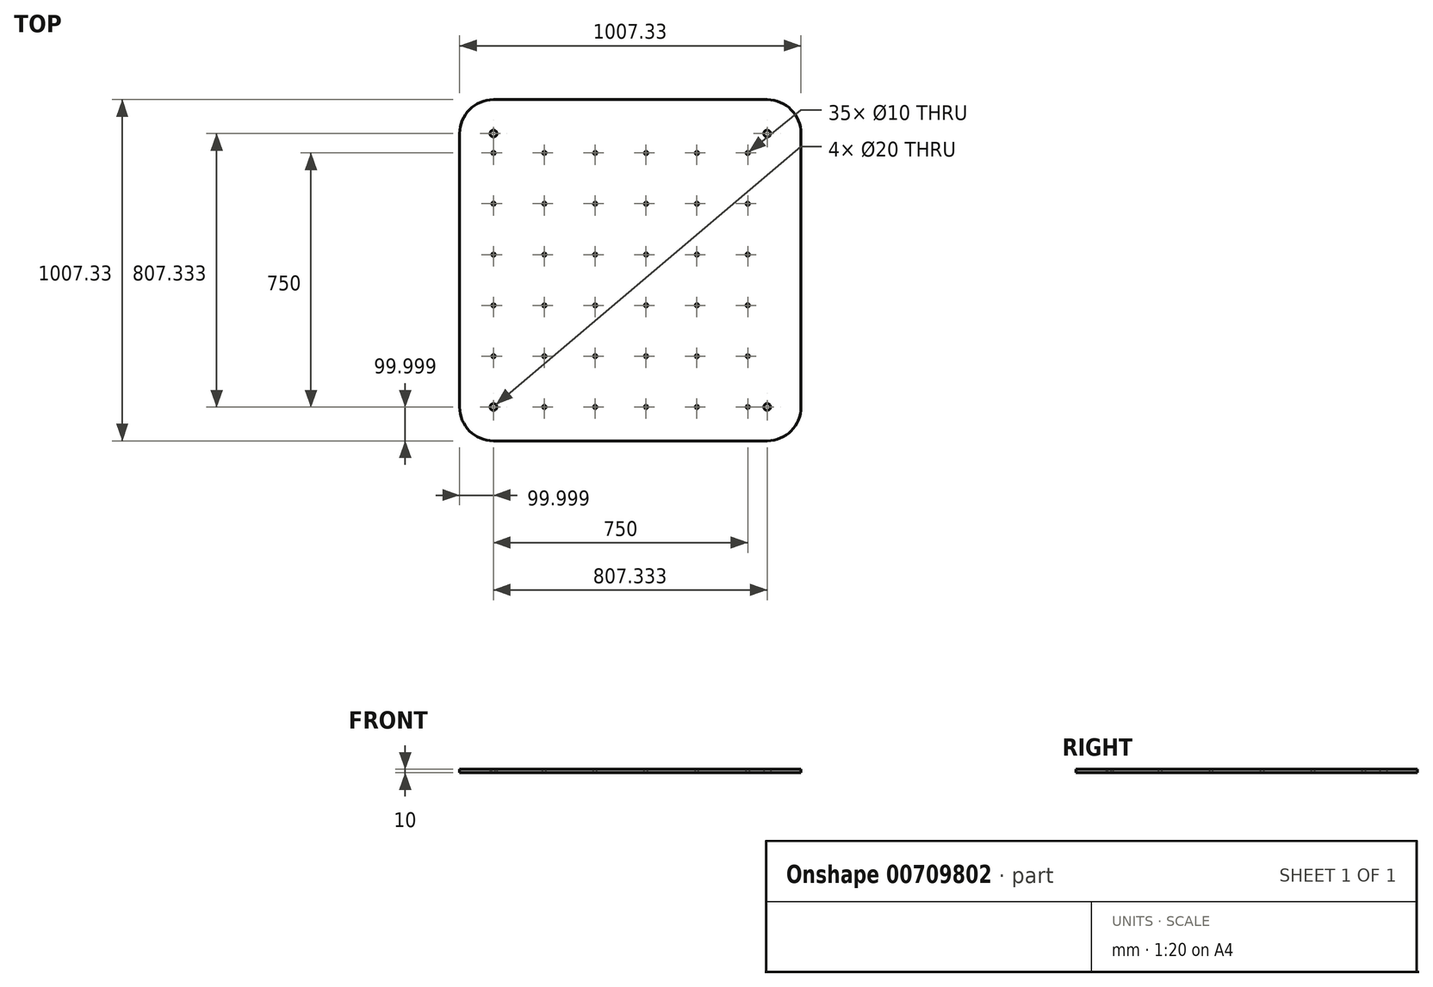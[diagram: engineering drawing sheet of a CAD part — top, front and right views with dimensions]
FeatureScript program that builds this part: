
annotation { "Feature Type Name" : "Feature", "Feature Type Description" : "" }
export const myFeature = defineFeature(function(context is Context, id is Id, definition is map)
    precondition{}
    {
        {
            var Q0;
            Q0=qCreatedBy(makeId("Top.planeOp"),FACE);
            var sketch = newSketch(context, id + "F0", { "sketchPlane" : qUnion([Q0])});
            skLineSegment(sketch, "E0.bottom", {"start": v(-368.41, -251.86) * mm, "end": v(438.92, -251.86) * mm});
            skLineSegment(sketch, "E0.top", {"start": v(-368.41, 555.47) * mm, "end": v(438.92, 555.47) * mm});
            skLineSegment(sketch, "E0.left", {"start": v(-368.41, -251.86) * mm, "end": v(-368.41, 555.47) * mm});
            skLineSegment(sketch, "E0.right", {"start": v(438.92, -251.86) * mm, "end": v(438.92, 555.47) * mm});
            skCircle(sketch, "E1", {"center": v(-368.41, 555.47) * mm, "radius": 10 * mm});
            skCircle(sketch, "E2", {"center": v(-368.41, -251.86) * mm, "radius": 10 * mm});
            skCircle(sketch, "E3", {"center": v(438.92, -251.86) * mm, "radius": 10 * mm});
            skCircle(sketch, "E4", {"center": v(438.92, 555.47) * mm, "radius": 10 * mm});
            skLineSegment(sketch, "E5.0", {"start": v(-468.41, -251.86) * mm, "end": v(-468.41, 555.47) * mm});
            skLineSegment(sketch, "E5.1", {"start": v(-368.41, -351.86) * mm, "end": v(438.92, -351.86) * mm});
            skLineSegment(sketch, "E5.2", {"start": v(538.92, -251.86) * mm, "end": v(538.92, 555.47) * mm});
            skLineSegment(sketch, "E5.3", {"start": v(-368.41, 655.47) * mm, "end": v(438.92, 655.47) * mm});
            skPoint(sketch, "E6.visualSharp", {"position": v(-468.41, 655.47) * mm});
            skArc(sketch, "E6.filletArc", {"start": v(-368.41, 655.47) * mm, "mid": v(-439.12, 626.18) * mm, "end": v(-468.41, 555.47) * mm});
            skPoint(sketch, "E7.visualSharp", {"position": v(538.92, 655.47) * mm});
            skArc(sketch, "E7.filletArc", {"start": v(538.92, 555.47) * mm, "mid": v(509.63, 626.18) * mm, "end": v(438.92, 655.47) * mm});
            skPoint(sketch, "E8.visualSharp", {"position": v(538.92, -351.86) * mm});
            skArc(sketch, "E8.filletArc", {"start": v(438.92, -351.86) * mm, "mid": v(509.63, -322.57) * mm, "end": v(538.92, -251.86) * mm});
            skPoint(sketch, "E9.visualSharp", {"position": v(-468.41, -351.86) * mm});
            skArc(sketch, "E9.filletArc", {"start": v(-468.41, -251.86) * mm, "mid": v(-439.12, -322.57) * mm, "end": v(-368.41, -351.86) * mm});
            skSolve(sketch);
        }
        {
            var Q0;
            Q0=makeQuery(id+"F0.imprint","IMPRINT",FACE,{"disambiguationData":[TD([[makeQuery(id+"F0.imprint","IMPRINT",EDGE,{"derivedFrom":sQuery(id+"F0.wireOp",EDGE,"E5.0")}),-1.0]])]});
            var Q1;
            {var subQ5=sQuery(id+"F0.wireOp",EDGE,"E2");var subQ13=sQuery(id+"F0.wireOp",EDGE,"E0.bottom");var subQ14=makeQuery(id+"F0.imprint","INTERSECT",VERTEX,{"derivedFrom":[subQ13,subQ5]});Q1=makeQuery(id+"F0.imprint","IMPRINT",FACE,{"disambiguationData":[TD([[makeQuery(id+"F0.imprint","IMPRINT",EDGE,{"disambiguationData":[TD([[subQ14,-1.0]])],"derivedFrom":subQ13}),1.0]])]});}
            extrude(context, id + "F1", {"entities" : qUnion([Q0, Q1]), "depth" : 10 * mm, "offsetDistance" : 25 * mm});
        }
        {
            var Q0;
            Q0=makeQuery(id+"F1.opExtrude","CAP_FACE",FACE,{"disambiguationData":[OSD([sQuery(id+"F0.wireOp",EDGE,"E1"),sQuery(id+"F0.wireOp",EDGE,"E2"),sQuery(id+"F0.wireOp",EDGE,"E3"),sQuery(id+"F0.wireOp",EDGE,"E4"),sQuery(id+"F0.wireOp",EDGE,"E5.0"),sQuery(id+"F0.wireOp",EDGE,"E5.1"),sQuery(id+"F0.wireOp",EDGE,"E5.2"),sQuery(id+"F0.wireOp",EDGE,"E5.3"),sQuery(id+"F0.wireOp",EDGE,"E6.filletArc"),sQuery(id+"F0.wireOp",EDGE,"E7.filletArc"),sQuery(id+"F0.wireOp",EDGE,"E8.filletArc"),sQuery(id+"F0.wireOp",EDGE,"E9.filletArc")])],"isStart":false});
            var sketch = newSketch(context, id + "F2", { "sketchPlane" : qUnion([Q0])});
            skLineSegment(sketch, "E10", {"start": v(-368.41, -251.86) * mm, "end": v(-218.41, -251.86) * mm});
            skCircle(sketch, "E11", {"center": v(-218.41, -251.86) * mm, "radius": 5 * mm});
            skCircle(sketch, "E12.0.1.0", {"center": v(-218.41, -101.86) * mm, "radius": 5 * mm});
            skCircle(sketch, "E12.0.2.0", {"center": v(-218.41, 48.14) * mm, "radius": 5 * mm});
            skCircle(sketch, "E12.0.3.0", {"center": v(-218.41, 198.14) * mm, "radius": 5 * mm});
            skCircle(sketch, "E12.0.4.0", {"center": v(-218.41, 348.14) * mm, "radius": 5 * mm});
            skCircle(sketch, "E12.0.5.0", {"center": v(-218.41, 498.14) * mm, "radius": 5 * mm});
            skCircle(sketch, "E12.1.0.0", {"center": v(-68.41, -251.86) * mm, "radius": 5 * mm});
            skCircle(sketch, "E12.1.1.0", {"center": v(-68.41, -101.86) * mm, "radius": 5 * mm});
            skCircle(sketch, "E12.1.2.0", {"center": v(-68.41, 48.14) * mm, "radius": 5 * mm});
            skCircle(sketch, "E12.1.3.0", {"center": v(-68.41, 198.14) * mm, "radius": 5 * mm});
            skCircle(sketch, "E12.1.4.0", {"center": v(-68.41, 348.14) * mm, "radius": 5 * mm});
            skCircle(sketch, "E12.1.5.0", {"center": v(-68.41, 498.14) * mm, "radius": 5 * mm});
            skCircle(sketch, "E12.2.0.0", {"center": v(81.59, -251.86) * mm, "radius": 5 * mm});
            skCircle(sketch, "E12.2.1.0", {"center": v(81.59, -101.86) * mm, "radius": 5 * mm});
            skCircle(sketch, "E12.2.2.0", {"center": v(81.59, 48.14) * mm, "radius": 5 * mm});
            skCircle(sketch, "E12.2.3.0", {"center": v(81.59, 198.14) * mm, "radius": 5 * mm});
            skCircle(sketch, "E12.2.4.0", {"center": v(81.59, 348.14) * mm, "radius": 5 * mm});
            skCircle(sketch, "E12.2.5.0", {"center": v(81.59, 498.14) * mm, "radius": 5 * mm});
            skCircle(sketch, "E12.3.0.0", {"center": v(231.59, -251.86) * mm, "radius": 5 * mm});
            skCircle(sketch, "E12.3.1.0", {"center": v(231.59, -101.86) * mm, "radius": 5 * mm});
            skCircle(sketch, "E12.3.2.0", {"center": v(231.59, 48.14) * mm, "radius": 5 * mm});
            skCircle(sketch, "E12.3.3.0", {"center": v(231.59, 198.14) * mm, "radius": 5 * mm});
            skCircle(sketch, "E12.3.4.0", {"center": v(231.59, 348.14) * mm, "radius": 5 * mm});
            skCircle(sketch, "E12.3.5.0", {"center": v(231.59, 498.14) * mm, "radius": 5 * mm});
            skCircle(sketch, "E12.4.0.0", {"center": v(381.59, -251.86) * mm, "radius": 5 * mm});
            skCircle(sketch, "E12.4.1.0", {"center": v(381.59, -101.86) * mm, "radius": 5 * mm});
            skCircle(sketch, "E12.4.2.0", {"center": v(381.59, 48.14) * mm, "radius": 5 * mm});
            skCircle(sketch, "E12.4.3.0", {"center": v(381.59, 198.14) * mm, "radius": 5 * mm});
            skCircle(sketch, "E12.4.4.0", {"center": v(381.59, 348.14) * mm, "radius": 5 * mm});
            skCircle(sketch, "E12.4.5.0", {"center": v(381.59, 498.14) * mm, "radius": 5 * mm});
            skLineSegment(sketch, "E12.direction1", {"start": v(-218.41, -251.86) * mm, "end": v(-68.41, -251.86) * mm, "construction": true});
            skLineSegment(sketch, "E12.direction2", {"start": v(-218.41, -251.86) * mm, "end": v(-218.41, -101.86) * mm, "construction": true});
            skCircle(sketch, "E13.1.0.0", {"center": v(-368.41, 498.14) * mm, "radius": 5 * mm});
            skCircle(sketch, "E13.1.0.1", {"center": v(-368.41, 348.14) * mm, "radius": 5 * mm});
            skCircle(sketch, "E13.1.0.2", {"center": v(-368.41, 198.14) * mm, "radius": 5 * mm});
            skCircle(sketch, "E13.1.0.3", {"center": v(-368.41, 48.14) * mm, "radius": 5 * mm});
            skCircle(sketch, "E13.1.0.4", {"center": v(-368.41, -101.86) * mm, "radius": 5 * mm});
            skLineSegment(sketch, "E13.direction1", {"start": v(-218.41, 498.14) * mm, "end": v(-368.41, 498.14) * mm, "construction": true});
            skSolve(sketch);
        }
        {
            var Q0;
            Q0=makeQuery(id+"F2.imprint","IMPRINT",FACE,{"disambiguationData":[TD([[makeQuery(id+"F2.imprint","IMPRINT",EDGE,{"derivedFrom":sQuery(id+"F2.wireOp",EDGE,"E13.1.0.4")}),1.0]])]});
            var Q1;
            Q1=makeQuery(id+"F2.imprint","IMPRINT",FACE,{"disambiguationData":[TD([[makeQuery(id+"F2.imprint","IMPRINT",EDGE,{"derivedFrom":sQuery(id+"F2.wireOp",EDGE,"E13.1.0.3")}),1.0]])]});
            var Q2;
            Q2=makeQuery(id+"F2.imprint","IMPRINT",FACE,{"disambiguationData":[TD([[makeQuery(id+"F2.imprint","IMPRINT",EDGE,{"derivedFrom":sQuery(id+"F2.wireOp",EDGE,"E12.0.2.0")}),1.0]])]});
            var Q3;
            Q3=makeQuery(id+"F2.imprint","IMPRINT",FACE,{"disambiguationData":[TD([[makeQuery(id+"F2.imprint","IMPRINT",EDGE,{"derivedFrom":sQuery(id+"F2.wireOp",EDGE,"E12.0.1.0")}),1.0]])]});
            var Q4;
            Q4=makeQuery(id+"F2.imprint","IMPRINT",FACE,{"disambiguationData":[TD([[makeQuery(id+"F2.imprint","IMPRINT",EDGE,{"derivedFrom":sQuery(id+"F2.wireOp",EDGE,"E11")}),1.0]])]});
            var Q5;
            Q5=makeQuery(id+"F2.imprint","IMPRINT",FACE,{"disambiguationData":[TD([[makeQuery(id+"F2.imprint","IMPRINT",EDGE,{"derivedFrom":sQuery(id+"F2.wireOp",EDGE,"E12.1.0.0")}),1.0]])]});
            var Q6;
            Q6=makeQuery(id+"F2.imprint","IMPRINT",FACE,{"disambiguationData":[TD([[makeQuery(id+"F2.imprint","IMPRINT",EDGE,{"derivedFrom":sQuery(id+"F2.wireOp",EDGE,"E12.2.0.0")}),1.0]])]});
            var Q7;
            Q7=makeQuery(id+"F2.imprint","IMPRINT",FACE,{"disambiguationData":[TD([[makeQuery(id+"F2.imprint","IMPRINT",EDGE,{"derivedFrom":sQuery(id+"F2.wireOp",EDGE,"E12.1.1.0")}),1.0]])]});
            var Q8;
            Q8=makeQuery(id+"F2.imprint","IMPRINT",FACE,{"disambiguationData":[TD([[makeQuery(id+"F2.imprint","IMPRINT",EDGE,{"derivedFrom":sQuery(id+"F2.wireOp",EDGE,"E12.1.2.0")}),1.0]])]});
            var Q9;
            Q9=makeQuery(id+"F2.imprint","IMPRINT",FACE,{"disambiguationData":[TD([[makeQuery(id+"F2.imprint","IMPRINT",EDGE,{"derivedFrom":sQuery(id+"F2.wireOp",EDGE,"E12.2.1.0")}),1.0]])]});
            var Q10;
            Q10=makeQuery(id+"F2.imprint","IMPRINT",FACE,{"disambiguationData":[TD([[makeQuery(id+"F2.imprint","IMPRINT",EDGE,{"derivedFrom":sQuery(id+"F2.wireOp",EDGE,"E13.1.0.2")}),1.0]])]});
            var Q11;
            Q11=makeQuery(id+"F2.imprint","IMPRINT",FACE,{"disambiguationData":[TD([[makeQuery(id+"F2.imprint","IMPRINT",EDGE,{"derivedFrom":sQuery(id+"F2.wireOp",EDGE,"E12.0.3.0")}),1.0]])]});
            var Q12;
            Q12=makeQuery(id+"F2.imprint","IMPRINT",FACE,{"disambiguationData":[TD([[makeQuery(id+"F2.imprint","IMPRINT",EDGE,{"derivedFrom":sQuery(id+"F2.wireOp",EDGE,"E12.1.3.0")}),1.0]])]});
            var Q13;
            Q13=makeQuery(id+"F2.imprint","IMPRINT",FACE,{"disambiguationData":[TD([[makeQuery(id+"F2.imprint","IMPRINT",EDGE,{"derivedFrom":sQuery(id+"F2.wireOp",EDGE,"E12.2.3.0")}),1.0]])]});
            var Q14;
            Q14=makeQuery(id+"F2.imprint","IMPRINT",FACE,{"disambiguationData":[TD([[makeQuery(id+"F2.imprint","IMPRINT",EDGE,{"derivedFrom":sQuery(id+"F2.wireOp",EDGE,"E12.2.2.0")}),1.0]])]});
            var Q15;
            Q15=makeQuery(id+"F2.imprint","IMPRINT",FACE,{"disambiguationData":[TD([[makeQuery(id+"F2.imprint","IMPRINT",EDGE,{"derivedFrom":sQuery(id+"F2.wireOp",EDGE,"E12.0.4.0")}),1.0]])]});
            var Q16;
            Q16=makeQuery(id+"F2.imprint","IMPRINT",FACE,{"disambiguationData":[TD([[makeQuery(id+"F2.imprint","IMPRINT",EDGE,{"derivedFrom":sQuery(id+"F2.wireOp",EDGE,"E13.1.0.1")}),1.0]])]});
            var Q17;
            Q17=makeQuery(id+"F2.imprint","IMPRINT",FACE,{"disambiguationData":[TD([[makeQuery(id+"F2.imprint","IMPRINT",EDGE,{"derivedFrom":sQuery(id+"F2.wireOp",EDGE,"E13.1.0.0")}),1.0]])]});
            var Q18;
            Q18=makeQuery(id+"F2.imprint","IMPRINT",FACE,{"disambiguationData":[TD([[makeQuery(id+"F2.imprint","IMPRINT",EDGE,{"derivedFrom":sQuery(id+"F2.wireOp",EDGE,"E12.0.5.0")}),1.0]])]});
            var Q19;
            Q19=makeQuery(id+"F2.imprint","IMPRINT",FACE,{"disambiguationData":[TD([[makeQuery(id+"F2.imprint","IMPRINT",EDGE,{"derivedFrom":sQuery(id+"F2.wireOp",EDGE,"E12.1.4.0")}),1.0]])]});
            var Q20;
            Q20=makeQuery(id+"F2.imprint","IMPRINT",FACE,{"disambiguationData":[TD([[makeQuery(id+"F2.imprint","IMPRINT",EDGE,{"derivedFrom":sQuery(id+"F2.wireOp",EDGE,"E12.1.5.0")}),1.0]])]});
            var Q21;
            Q21=makeQuery(id+"F2.imprint","IMPRINT",FACE,{"disambiguationData":[TD([[makeQuery(id+"F2.imprint","IMPRINT",EDGE,{"derivedFrom":sQuery(id+"F2.wireOp",EDGE,"E12.2.4.0")}),1.0]])]});
            var Q22;
            Q22=makeQuery(id+"F2.imprint","IMPRINT",FACE,{"disambiguationData":[TD([[makeQuery(id+"F2.imprint","IMPRINT",EDGE,{"derivedFrom":sQuery(id+"F2.wireOp",EDGE,"E12.2.5.0")}),1.0]])]});
            var Q23;
            Q23=makeQuery(id+"F2.imprint","IMPRINT",FACE,{"disambiguationData":[TD([[makeQuery(id+"F2.imprint","IMPRINT",EDGE,{"derivedFrom":sQuery(id+"F2.wireOp",EDGE,"E12.3.4.0")}),1.0]])]});
            var Q24;
            Q24=makeQuery(id+"F2.imprint","IMPRINT",FACE,{"disambiguationData":[TD([[makeQuery(id+"F2.imprint","IMPRINT",EDGE,{"derivedFrom":sQuery(id+"F2.wireOp",EDGE,"E12.3.5.0")}),1.0]])]});
            var Q25;
            Q25=makeQuery(id+"F2.imprint","IMPRINT",FACE,{"disambiguationData":[TD([[makeQuery(id+"F2.imprint","IMPRINT",EDGE,{"derivedFrom":sQuery(id+"F2.wireOp",EDGE,"E12.4.5.0")}),1.0]])]});
            var Q26;
            Q26=makeQuery(id+"F2.imprint","IMPRINT",FACE,{"disambiguationData":[TD([[makeQuery(id+"F2.imprint","IMPRINT",EDGE,{"derivedFrom":sQuery(id+"F2.wireOp",EDGE,"E12.4.4.0")}),1.0]])]});
            var Q27;
            Q27=makeQuery(id+"F2.imprint","IMPRINT",FACE,{"disambiguationData":[TD([[makeQuery(id+"F2.imprint","IMPRINT",EDGE,{"derivedFrom":sQuery(id+"F2.wireOp",EDGE,"E12.3.3.0")}),1.0]])]});
            var Q28;
            Q28=makeQuery(id+"F2.imprint","IMPRINT",FACE,{"disambiguationData":[TD([[makeQuery(id+"F2.imprint","IMPRINT",EDGE,{"derivedFrom":sQuery(id+"F2.wireOp",EDGE,"E12.4.3.0")}),1.0]])]});
            var Q29;
            Q29=makeQuery(id+"F2.imprint","IMPRINT",FACE,{"disambiguationData":[TD([[makeQuery(id+"F2.imprint","IMPRINT",EDGE,{"derivedFrom":sQuery(id+"F2.wireOp",EDGE,"E12.4.2.0")}),1.0]])]});
            var Q30;
            Q30=makeQuery(id+"F2.imprint","IMPRINT",FACE,{"disambiguationData":[TD([[makeQuery(id+"F2.imprint","IMPRINT",EDGE,{"derivedFrom":sQuery(id+"F2.wireOp",EDGE,"E12.3.2.0")}),1.0]])]});
            var Q31;
            Q31=makeQuery(id+"F2.imprint","IMPRINT",FACE,{"disambiguationData":[TD([[makeQuery(id+"F2.imprint","IMPRINT",EDGE,{"derivedFrom":sQuery(id+"F2.wireOp",EDGE,"E12.3.1.0")}),1.0]])]});
            var Q32;
            Q32=makeQuery(id+"F2.imprint","IMPRINT",FACE,{"disambiguationData":[TD([[makeQuery(id+"F2.imprint","IMPRINT",EDGE,{"derivedFrom":sQuery(id+"F2.wireOp",EDGE,"E12.4.1.0")}),1.0]])]});
            var Q33;
            Q33=makeQuery(id+"F2.imprint","IMPRINT",FACE,{"disambiguationData":[TD([[makeQuery(id+"F2.imprint","IMPRINT",EDGE,{"derivedFrom":sQuery(id+"F2.wireOp",EDGE,"E12.4.0.0")}),1.0]])]});
            var Q34;
            Q34=makeQuery(id+"F2.imprint","IMPRINT",FACE,{"disambiguationData":[TD([[makeQuery(id+"F2.imprint","IMPRINT",EDGE,{"derivedFrom":sQuery(id+"F2.wireOp",EDGE,"E12.3.0.0")}),1.0]])]});
            var Q35;
            Q35=makeQuery(id+"F1.opExtrude","CAP_FACE",FACE,{"disambiguationData":[OSD([sQuery(id+"F0.wireOp",EDGE,"E1"),sQuery(id+"F0.wireOp",EDGE,"E2"),sQuery(id+"F0.wireOp",EDGE,"E3"),sQuery(id+"F0.wireOp",EDGE,"E4"),sQuery(id+"F0.wireOp",EDGE,"E5.0"),sQuery(id+"F0.wireOp",EDGE,"E5.1"),sQuery(id+"F0.wireOp",EDGE,"E5.2"),sQuery(id+"F0.wireOp",EDGE,"E5.3"),sQuery(id+"F0.wireOp",EDGE,"E6.filletArc"),sQuery(id+"F0.wireOp",EDGE,"E7.filletArc"),sQuery(id+"F0.wireOp",EDGE,"E8.filletArc"),sQuery(id+"F0.wireOp",EDGE,"E9.filletArc")])],"isStart":true});
            extrude(context, id + "F3", {"entities" : qUnion([Q0, Q1, Q2, Q3, Q4, Q5, Q6, Q7, Q8, Q9, Q10, Q11, Q12, Q13, Q14, Q15, Q16, Q17, Q18, Q19, Q20, Q21, Q22, Q23, Q24, Q25, Q26, Q27, Q28, Q29, Q30, Q31, Q32, Q33, Q34]), "operationType" : NewBodyOperationType.REMOVE, "oppositeDirection" : true, "depth" : 25 * mm, "endBoundEntityFace" : qUnion([Q35]), "offsetDistance" : 25 * mm});
        }
    });
